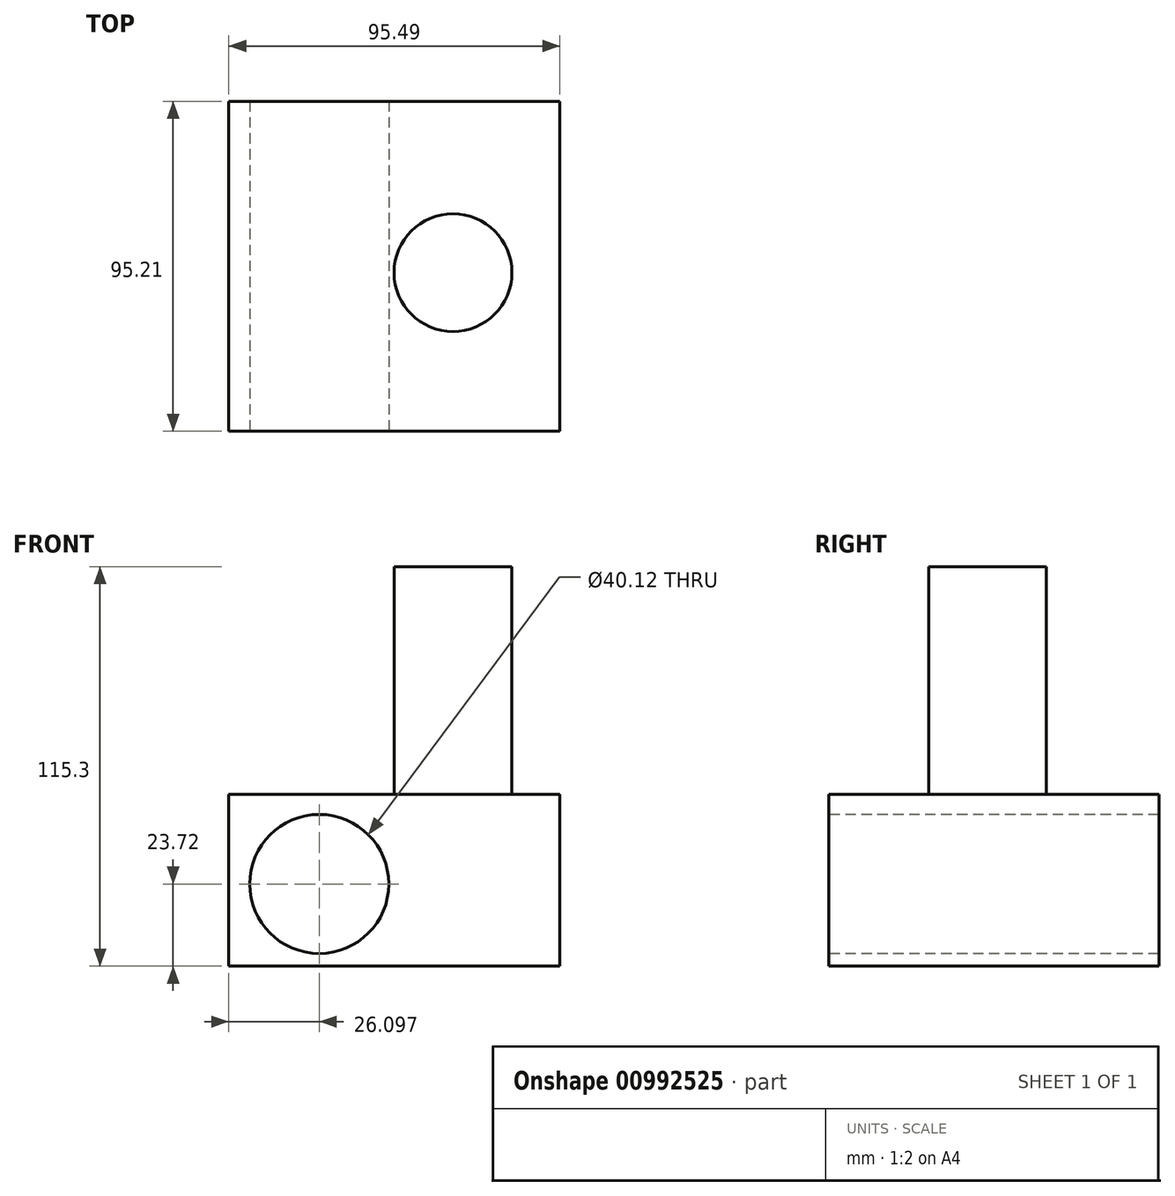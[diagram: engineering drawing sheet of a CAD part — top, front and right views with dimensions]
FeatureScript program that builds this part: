
annotation { "Feature Type Name" : "Feature", "Feature Type Description" : "" }
export const myFeature = defineFeature(function(context is Context, id is Id, definition is map)
    precondition{}
    {
        {
            var Q0;
            Q0=qCreatedBy(makeId("Front.planeOp"),FACE);
            var sketch = newSketch(context, id + "F0", { "sketchPlane" : qUnion([Q0])});
            skLineSegment(sketch, "E0.bottom", {"start": v(-35.14, 25.92) * mm, "end": v(60.35, 25.92) * mm});
            skLineSegment(sketch, "E0.top", {"start": v(-35.14, -23.72) * mm, "end": v(60.35, -23.72) * mm});
            skLineSegment(sketch, "E0.left", {"start": v(-35.14, 25.92) * mm, "end": v(-35.14, -23.72) * mm});
            skLineSegment(sketch, "E0.right", {"start": v(60.35, 25.92) * mm, "end": v(60.35, -23.72) * mm});
            skCircle(sketch, "E1", {"center": v(-9.04, 0) * mm, "radius": 20.06 * mm});
            skCircle(sketch, "E2", {"center": v(-9.04, 0) * mm, "radius": 12.3 * mm});
            skSolve(sketch);
        }
        {
            var Q0;
            Q0=makeQuery(id+"F0.imprint","IMPRINT",FACE,{"disambiguationData":[TD([[makeQuery(id+"F0.imprint","IMPRINT",EDGE,{"derivedFrom":sQuery(id+"F0.wireOp",EDGE,"E0.bottom")}),-1.0]])]});
            extrude(context, id + "F1", {"entities" : qUnion([Q0]), "oppositeDirection" : true, "depth" : 95.2 * mm, "offsetDistance" : 25.4 * mm});
        }
        {
            var Q0;
            Q0=makeQuery(id+"F1.opExtrude","SWEPT_FACE",FACE,{"disambiguationData":[OSD([sQuery(id+"F0.wireOp",EDGE,"E0.bottom")])]});
            var sketch = newSketch(context, id + "F2", { "sketchPlane" : qUnion([Q0])});
            skCircle(sketch, "E3", {"center": v(29.53, 45.79) * mm, "radius": 16.99 * mm});
            skSolve(sketch);
        }
        {
            var Q0;
            Q0=makeQuery(id+"F2.imprint","IMPRINT",FACE,{"disambiguationData":[TD([[makeQuery(id+"F2.imprint","IMPRINT",EDGE,{"derivedFrom":sQuery(id+"F2.wireOp",EDGE,"E3")}),1.0]])]});
            extrude(context, id + "F3", {"entities" : qUnion([Q0]), "operationType" : NewBodyOperationType.ADD, "depth" : 65.66 * mm, "offsetDistance" : 25.4 * mm});
        }
    });
